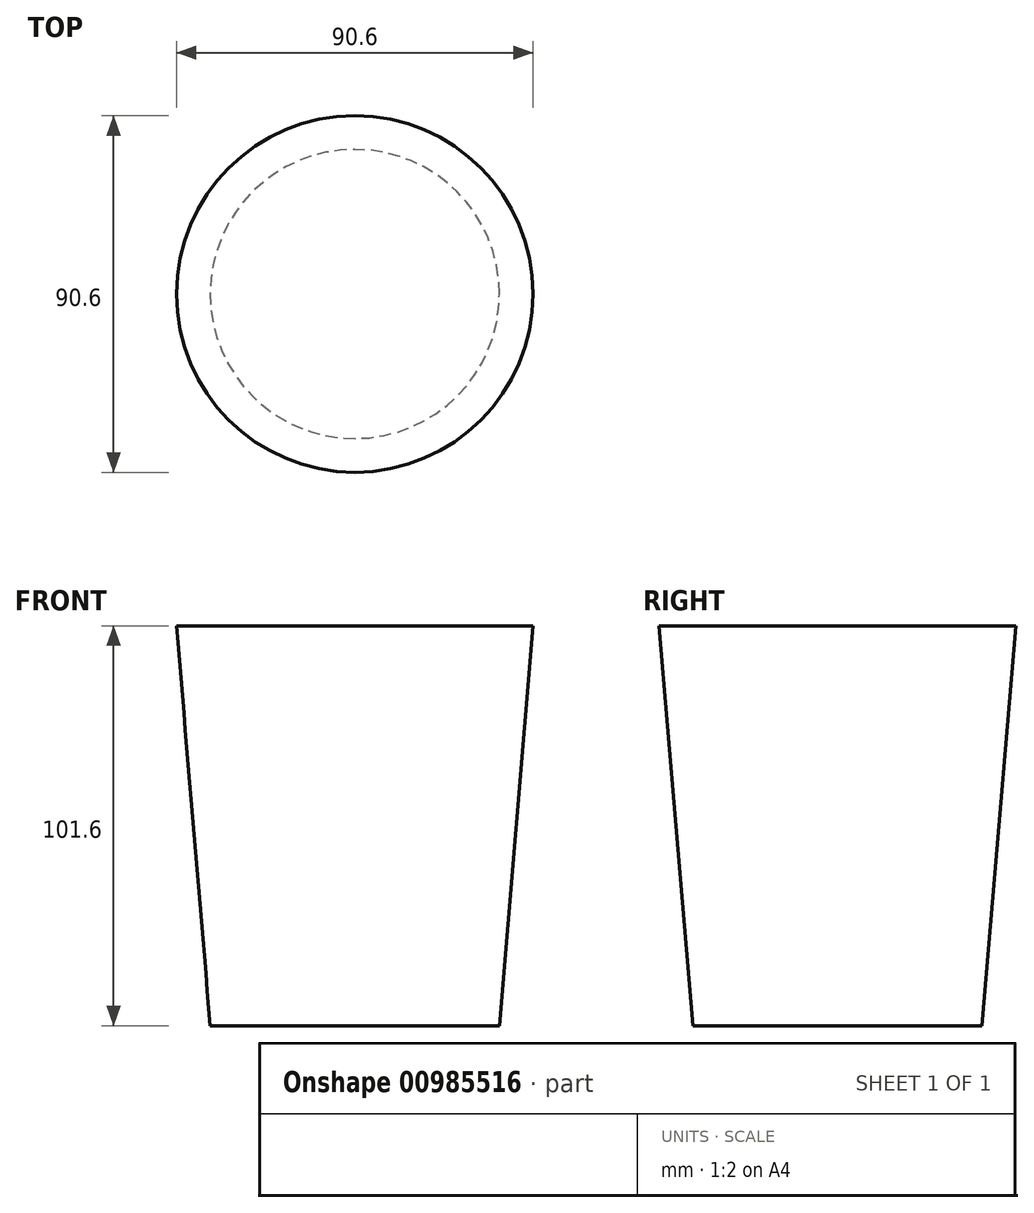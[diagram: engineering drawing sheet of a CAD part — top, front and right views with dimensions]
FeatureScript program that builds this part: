
annotation { "Feature Type Name" : "Feature", "Feature Type Description" : "" }
export const myFeature = defineFeature(function(context is Context, id is Id, definition is map)
    precondition{}
    {
        {
            var Q0;
            Q0=qCreatedBy(makeId("Front.planeOp"),FACE);
            var sketch = newSketch(context, id + "F0", { "sketchPlane" : qUnion([Q0])});
            skLineSegment(sketch, "E0", {"start": v(0, 0) * mm, "end": v(0, 101.6) * mm});
            skLineSegment(sketch, "E1", {"start": v(0, 101.6) * mm, "end": v(-45.3, 101.6) * mm});
            skLineSegment(sketch, "E2", {"start": v(-45.3, 101.6) * mm, "end": v(-36.73, 0) * mm});
            skLineSegment(sketch, "E3", {"start": v(-36.73, 0) * mm, "end": v(0, 0) * mm});
            skSolve(sketch);
        }
        {
            var Q0;
            Q0 = qSketchRegion(id + "F0", true);
            var Q1;
            Q1=sQuery(id+"F0.wireOp",EDGE,"E0");
            revolve(context, id + "F1", {"surfaceOperationType" : NewSurfaceOperationType.NEW, "entities" : qUnion([Q0]), "axis" : qUnion([Q1]), "revolveType" : RevolveType.FULL});
        }
    });
